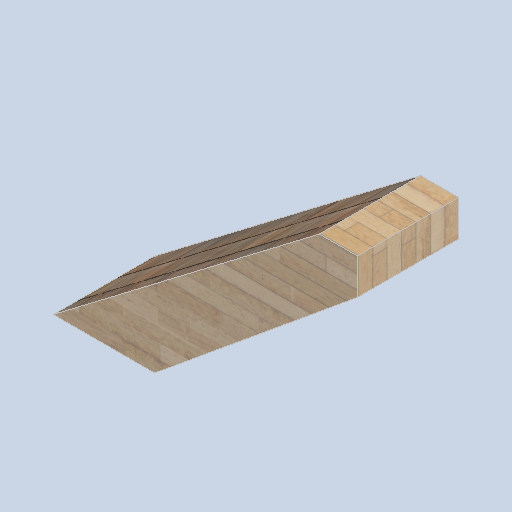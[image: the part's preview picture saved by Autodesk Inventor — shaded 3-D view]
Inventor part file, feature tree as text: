
AUTODESK INVENTOR PART (.ipt)
format: ipt  version: 2024.2 (Build 282272000, 272)  size: 161,280 bytes
history: native  units: in
note: dims shown in document units (in); Inventor stores cm internally (conversion verified against a paired STEP export)
features: other x3, sketch x1
ambient origin geometry x8: Origin, YZ Plane, XZ Plane, XY Plane, X Axis, Y Axis, Z Axis, Center Point
bodies: Body1 (feature_tree)
feature tree (4):
  other  "frame_rib_02_MIR.ipt"
  other  "Solid3::frame_rib_02_MIR.ipt"
  other  "TaggingFeature1"
  sketch  "Sketch1"  dims[d0=0.3937in]
